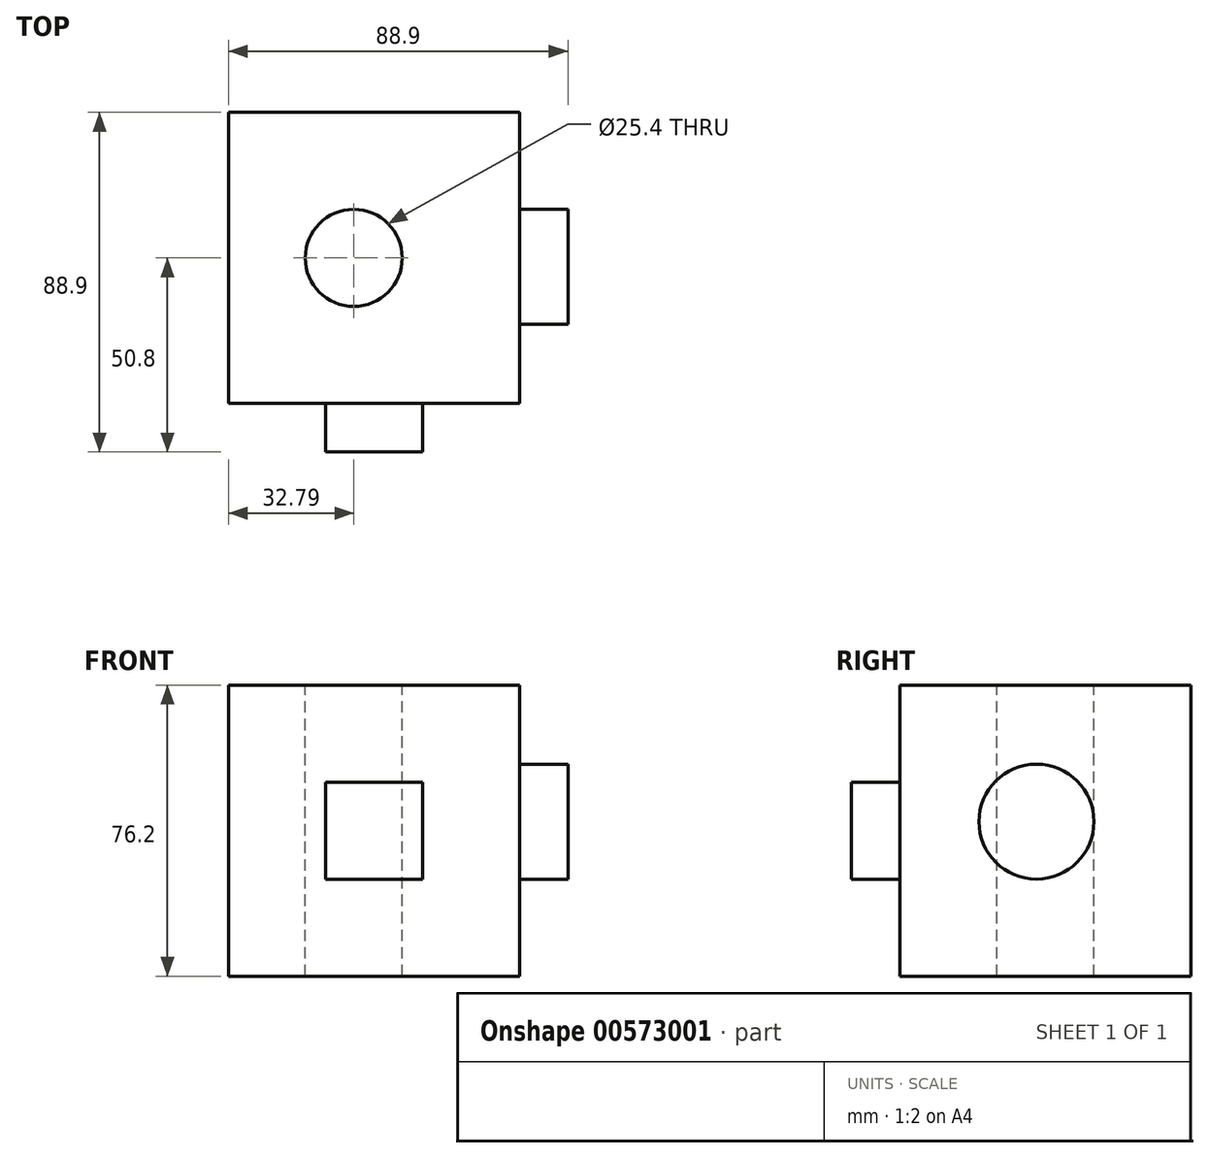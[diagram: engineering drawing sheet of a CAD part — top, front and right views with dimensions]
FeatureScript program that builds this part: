
annotation { "Feature Type Name" : "Feature", "Feature Type Description" : "" }
export const myFeature = defineFeature(function(context is Context, id is Id, definition is map)
    precondition{}
    {
        {
            var Q0;
            Q0=qCreatedBy(makeId("Front.planeOp"),FACE);
            var sketch = newSketch(context, id + "F0", { "sketchPlane" : qUnion([Q0])});
            skLineSegment(sketch, "E0.bottom", {"start": v(-32.8, -23.34) * mm, "end": v(43.4, -23.34) * mm});
            skLineSegment(sketch, "E0.top", {"start": v(-32.8, 52.86) * mm, "end": v(43.4, 52.86) * mm});
            skLineSegment(sketch, "E0.left", {"start": v(-32.8, -23.34) * mm, "end": v(-32.8, 52.86) * mm});
            skLineSegment(sketch, "E0.right", {"start": v(43.4, -23.34) * mm, "end": v(43.4, 52.86) * mm});
            skSolve(sketch);
        }
        {
            var Q0;
            Q0=makeQuery(id+"F0.imprint","IMPRINT",FACE,{"disambiguationData":[TD([[makeQuery(id+"F0.imprint","IMPRINT",EDGE,{"derivedFrom":sQuery(id+"F0.wireOp",EDGE,"E0.bottom")}),1.0]])]});
            extrude(context, id + "F1", {"entities" : qUnion([Q0]), "depth" : 76.2 * mm, "offsetDistance" : 25.4 * mm});
        }
        {
            var Q0;
            Q0=makeQuery(id+"F1.opExtrude","CAP_FACE",FACE,{"disambiguationData":[OSD([sQuery(id+"F0.wireOp",EDGE,"E0.bottom"),sQuery(id+"F0.wireOp",EDGE,"E0.top"),sQuery(id+"F0.wireOp",EDGE,"E0.left"),sQuery(id+"F0.wireOp",EDGE,"E0.right")])],"isStart":false});
            var sketch = newSketch(context, id + "F2", { "sketchPlane" : qUnion([Q0])});
            skLineSegment(sketch, "E1.bottom", {"start": v(-7.4, 2.06) * mm, "end": v(18, 2.06) * mm});
            skLineSegment(sketch, "E1.top", {"start": v(-7.4, 27.46) * mm, "end": v(18, 27.46) * mm});
            skLineSegment(sketch, "E1.left", {"start": v(-7.4, 2.06) * mm, "end": v(-7.4, 27.46) * mm});
            skLineSegment(sketch, "E1.right", {"start": v(18, 2.06) * mm, "end": v(18, 27.46) * mm});
            skSolve(sketch);
        }
        {
            var Q0;
            Q0=makeQuery(id+"F2.imprint","IMPRINT",FACE,{"disambiguationData":[TD([[makeQuery(id+"F2.imprint","IMPRINT",EDGE,{"derivedFrom":sQuery(id+"F2.wireOp",EDGE,"E1.bottom")}),1.0]])]});
            extrude(context, id + "F3", {"entities" : qUnion([Q0]), "operationType" : NewBodyOperationType.ADD, "depth" : 12.7 * mm, "offsetDistance" : 25.4 * mm});
        }
        {
            var Q0;
            Q0=makeQuery(id+"F1.opExtrude","SWEPT_FACE",FACE,{"disambiguationData":[OSD([sQuery(id+"F0.wireOp",EDGE,"E0.top")])]});
            var sketch = newSketch(context, id + "F4", { "sketchPlane" : qUnion([Q0])});
            skPoint(sketch, "E2", {"position": v(0, -38.1) * mm});
            skSolve(sketch);
        }
        {
            var Q0;
            Q0=sQuery(id+"F4.wireOp",VERTEX,"E2");
            var Q1;
            Q1=makeQuery(id+"F1.opExtrude","SWEPT_BODY",BODY,{"disambiguationData":[OSD([sQuery(id+"F0.wireOp",EDGE,"E0.bottom"),sQuery(id+"F0.wireOp",EDGE,"E0.top"),sQuery(id+"F0.wireOp",EDGE,"E0.left"),sQuery(id+"F0.wireOp",EDGE,"E0.right")])]});
            hole(context, id + "F5", {"style" : HoleStyle.SIMPLE, "endStyle" : HoleEndStyle.THROUGH, "holeDiameter" : 25.4 * mm, "isTappedThrough" : true, "tappedDepth" : 12.7 * mm, "tapClearance" : 3, "locations" : qUnion([Q0]), "scope" : qUnion([Q1])});
        }
        {
            var Q0;
            Q0=makeQuery(id+"F1.opExtrude","SWEPT_FACE",FACE,{"disambiguationData":[OSD([sQuery(id+"F0.wireOp",EDGE,"E0.right")])]});
            var sketch = newSketch(context, id + "F6", { "sketchPlane" : qUnion([Q0])});
            skCircle(sketch, "E3", {"center": v(-40.45, 17.1) * mm, "radius": 15.05 * mm});
            skSolve(sketch);
        }
        {
            var Q0;
            Q0=makeQuery(id+"F6.imprint","IMPRINT",FACE,{"disambiguationData":[TD([[makeQuery(id+"F6.imprint","IMPRINT",EDGE,{"derivedFrom":sQuery(id+"F6.wireOp",EDGE,"E3")}),1.0]])]});
            extrude(context, id + "F7", {"entities" : qUnion([Q0]), "operationType" : NewBodyOperationType.ADD, "depth" : 12.7 * mm, "offsetDistance" : 25.4 * mm});
        }
    });
